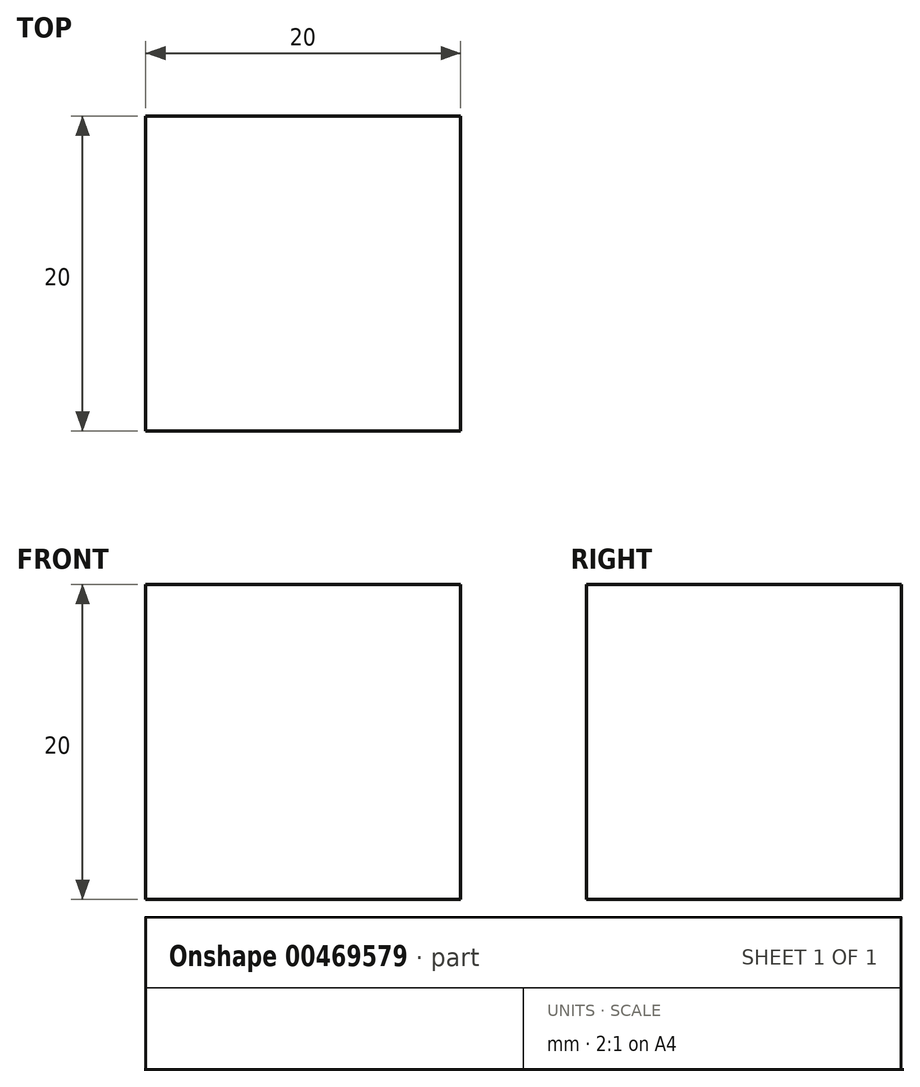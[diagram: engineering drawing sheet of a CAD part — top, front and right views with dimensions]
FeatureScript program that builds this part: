
annotation { "Feature Type Name" : "Feature", "Feature Type Description" : "" }
export const myFeature = defineFeature(function(context is Context, id is Id, definition is map)
    precondition{}
    {
        {
            var Q0;
            Q0=qCreatedBy(makeId("Front.planeOp"),FACE);
            var sketch = newSketch(context, id + "F0", { "sketchPlane" : qUnion([Q0])});
            skLineSegment(sketch, "E0.bottom", {"start": v(0, 0) * mm, "end": v(20, 0) * mm});
            skLineSegment(sketch, "E0.top", {"start": v(0, 20) * mm, "end": v(20, 20) * mm});
            skLineSegment(sketch, "E0.left", {"start": v(0, 0) * mm, "end": v(0, 20) * mm});
            skLineSegment(sketch, "E0.right", {"start": v(20, 0) * mm, "end": v(20, 20) * mm});
            skSolve(sketch);
        }
        {
            var Q0;
            Q0 = qSketchRegion(id + "F0", true);
            extrude(context, id + "F1", {"entities" : qUnion([Q0]), "depth" : 20 * mm});
        }
        {
            var Q0;
            Q0=makeQuery(id+"F1.opExtrude","CAP_FACE",FACE,{"disambiguationData":[OSD([sQuery(id+"F0.wireOp",EDGE,"E0.bottom"),sQuery(id+"F0.wireOp",EDGE,"E0.top"),sQuery(id+"F0.wireOp",EDGE,"E0.left"),sQuery(id+"F0.wireOp",EDGE,"E0.right")])],"isStart":false});
            var sketch = newSketch(context, id + "F2", { "sketchPlane" : qUnion([Q0])});
            skLineSegment(sketch, "E1", {"start": v(0, 20) * mm, "end": v(20, 0) * mm, "construction": true});
            skLineSegment(sketch, "E2", {"start": v(0, 0) * mm, "end": v(20, 20) * mm, "construction": true});
            skLineSegment(sketch, "E3", {"start": v(10, 20) * mm, "end": v(10, 0) * mm, "construction": true});
            skLineSegment(sketch, "E4", {"start": v(0, 10) * mm, "end": v(20, 10) * mm, "construction": true});
            skCircle(sketch, "E5", {"center": v(10, 10) * mm, "radius": 2.6 * mm, "construction": true});
            skCircle(sketch, "E6", {"center": v(10, 10) * mm, "radius": 2.6 * mm});
            skCircle(sketch, "E7", {"center": v(5, 15) * mm, "radius": 2.35 * mm});
            skLineSegment(sketch, "E8", {"start": v(0, 20) * mm, "end": v(5, 20) * mm, "construction": true});
            skSolve(sketch);
        }
    });
